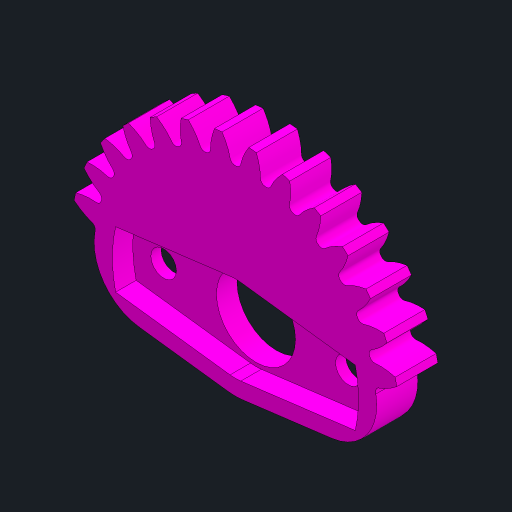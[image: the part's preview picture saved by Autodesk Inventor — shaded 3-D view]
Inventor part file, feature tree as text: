
AUTODESK INVENTOR PART (.ipt)
format: ipt  version: 2023.2 (Build 272271030, 271C)  size: 703,488 bytes
history: native  units: mm
features: sketch x5, extrude x5, pattern_circular x1, hole x1, projected_geometry x1
ambient origin geometry x8: Origin, YZ Plane, XZ Plane, XY Plane, X Axis, Y Axis, Z Axis, Center Point
bodies: Solid1 (feature_tree)
feature tree (13):
  sketch  "Sketch1"  dims[d0=4.0mm d1=0.0mm d2=0.0mm d3=0.0mm]
  extrude  "Extrusion1"  TaperAngle=0.0deg  [1 undecoded]
  extrude  "Extrusion2"  Depth=8.0mm
  pattern_circular  "Circular Pattern1"  [2 undecoded]
  extrude  "Extrusion3"  Depth=5.0mm
  extrude  "Extrusion4"  Depth=5.0mm
  hole  "Hole1"  [1 undecoded]
  extrude  "Extrusion5"  TaperAngle=0.0deg  [1 undecoded]
  sketch  "Sketch2"  dims[d4=300.0mm d5=360.0deg d7=8.0mm]
  sketch  "Sketch3"  dims[d8=32.0mm]
  sketch  "Sketch4"  dims[d9=4.0mm]
  sketch  "Sketch6"  dims[d10=4.0mm d11=4.0mm d12=0.2mm d13=24.0mm d14=2.0mm d15=0.0mm d16=0.0mm d17=0.0mm d18=18.0mm d19=9.0mm d20=2.5mm d21=6.0mm d22=6.0mm d23=1.0mm d24=90.0deg d25=8.0mm d26=20.594885mm d27=1.5mm d28=5.0mm d29=0.0mm d30=0.0mm d31=7.7mm]
  projected_geometry  "Projected Loop2"
note: 5 required parameter values undecoded (feature->parameter linkage not recoverable at this tier; creation-order binding heuristic only, values carry confidence <= 0.55)
